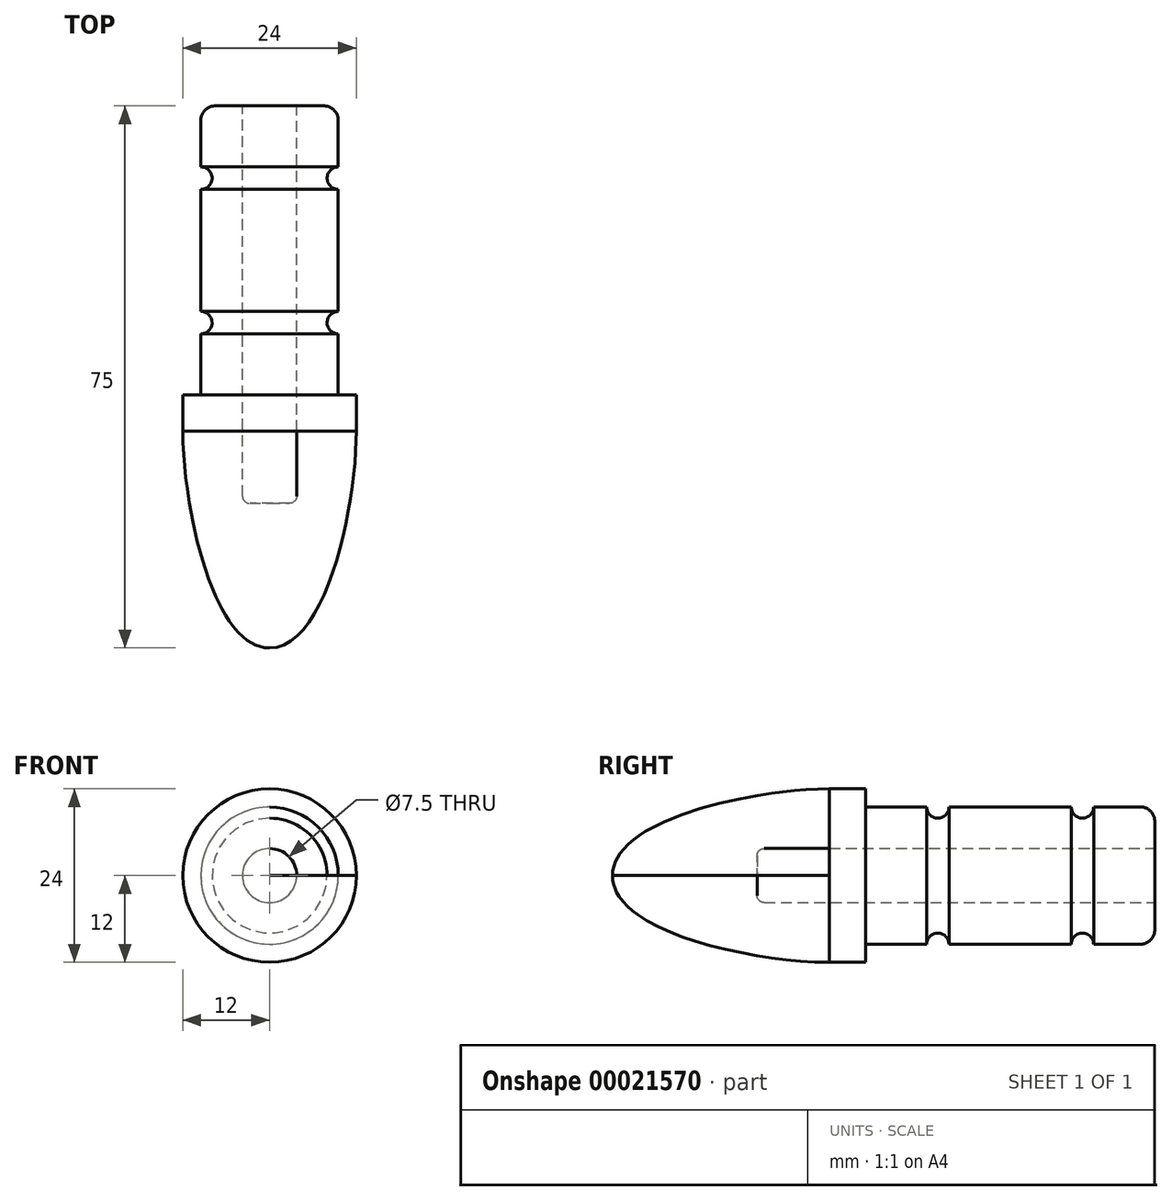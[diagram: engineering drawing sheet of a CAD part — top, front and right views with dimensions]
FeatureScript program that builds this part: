
annotation { "Feature Type Name" : "Feature", "Feature Type Description" : "" }
export const myFeature = defineFeature(function(context is Context, id is Id, definition is map)
    precondition{}
    {
        {
            var Q0;
            Q0=qCreatedBy(makeId("Top.planeOp"),FACE);
            var sketch = newSketch(context, id + "F0", { "sketchPlane" : qUnion([Q0])});
            skLineSegment(sketch, "E0", {"start": v(0, -55) * mm, "end": v(0, -75) * mm});
            skLineSegment(sketch, "E1", {"start": v(3.75, 0) * mm, "end": v(7.5, 0) * mm});
            skLineSegment(sketch, "E2", {"start": v(9.5, -2) * mm, "end": v(9.5, -40) * mm});
            skLineSegment(sketch, "E3", {"start": v(9.5, -40) * mm, "end": v(12, -40) * mm});
            skLineSegment(sketch, "E4", {"start": v(12, -40) * mm, "end": v(12, -45) * mm});
            skPoint(sketch, "E5", {"position": v(0, -75) * mm});
            skLineSegment(sketch, "E6", {"start": v(0, -75) * mm, "end": v(-13.94, -75) * mm, "construction": true});
            skFitSpline(sketch, "E7", {"points": [v(12, -45) * mm, v(0, -75) * mm], "startDerivative": vector(0, -30) * mm, "endDerivative": vector(-24, 0) * mm});
            skPoint(sketch, "E8.visualSharp", {"position": v(9.5, 0) * mm});
            skArc(sketch, "E8.filletArc", {"start": v(9.5, -2) * mm, "mid": v(8.91, -0.59) * mm, "end": v(7.5, 0) * mm});
            skLineSegment(sketch, "E9", {"start": v(3.75, 0) * mm, "end": v(3.75, -54) * mm});
            skLineSegment(sketch, "E10", {"start": v(2.75, -55) * mm, "end": v(0, -55) * mm});
            skPoint(sketch, "E11.orphan", {"position": v(0, 0) * mm});
            skLineSegment(sketch, "E12", {"start": v(0, -55) * mm, "end": v(0, 0) * mm, "construction": true});
            skPoint(sketch, "E13.visualSharp", {"position": v(3.75, -55) * mm});
            skArc(sketch, "E13.filletArc", {"start": v(2.75, -55) * mm, "mid": v(3.46, -54.7) * mm, "end": v(3.75, -54) * mm});
            skSolve(sketch);
        }
        {
            var Q0;
            Q0=makeQuery(id+"F0.imprint","IMPRINT",FACE,{"disambiguationData":[TD([[makeQuery(id+"F0.imprint","IMPRINT",EDGE,{"derivedFrom":sQuery(id+"F0.wireOp",EDGE,"E0")}),1.0]])]});
            var Q1;
            Q1=sQuery(id+"F0.wireOp",EDGE,"E0");
            revolve(context, id + "F1", {"entities" : qUnion([Q0]), "axis" : qUnion([Q1]), "revolveType" : RevolveType.FULL});
        }
        {
            var Q0;
            Q0=qCreatedBy(makeId("Top.planeOp"),FACE);
            var sketch = newSketch(context, id + "F2", { "sketchPlane" : qUnion([Q0])});
            skCircle(sketch, "E14", {"center": v(9.5, -30) * mm, "radius": 1.55 * mm});
            skCircle(sketch, "E15", {"center": v(9.5, -10) * mm, "radius": 1.55 * mm});
            skSolve(sketch);
        }
        {
            var Q0;
            Q0 = qSketchRegion(id + "F2", true);
            var Q1;
            Q1=sQuery(id+"F0.wireOp",EDGE,"E12");
            revolve(context, id + "F3", {"operationType" : NewBodyOperationType.REMOVE, "entities" : qUnion([Q0]), "axis" : qUnion([Q1]), "revolveType" : RevolveType.FULL, "oppositeDirection" : true});
        }
    });
